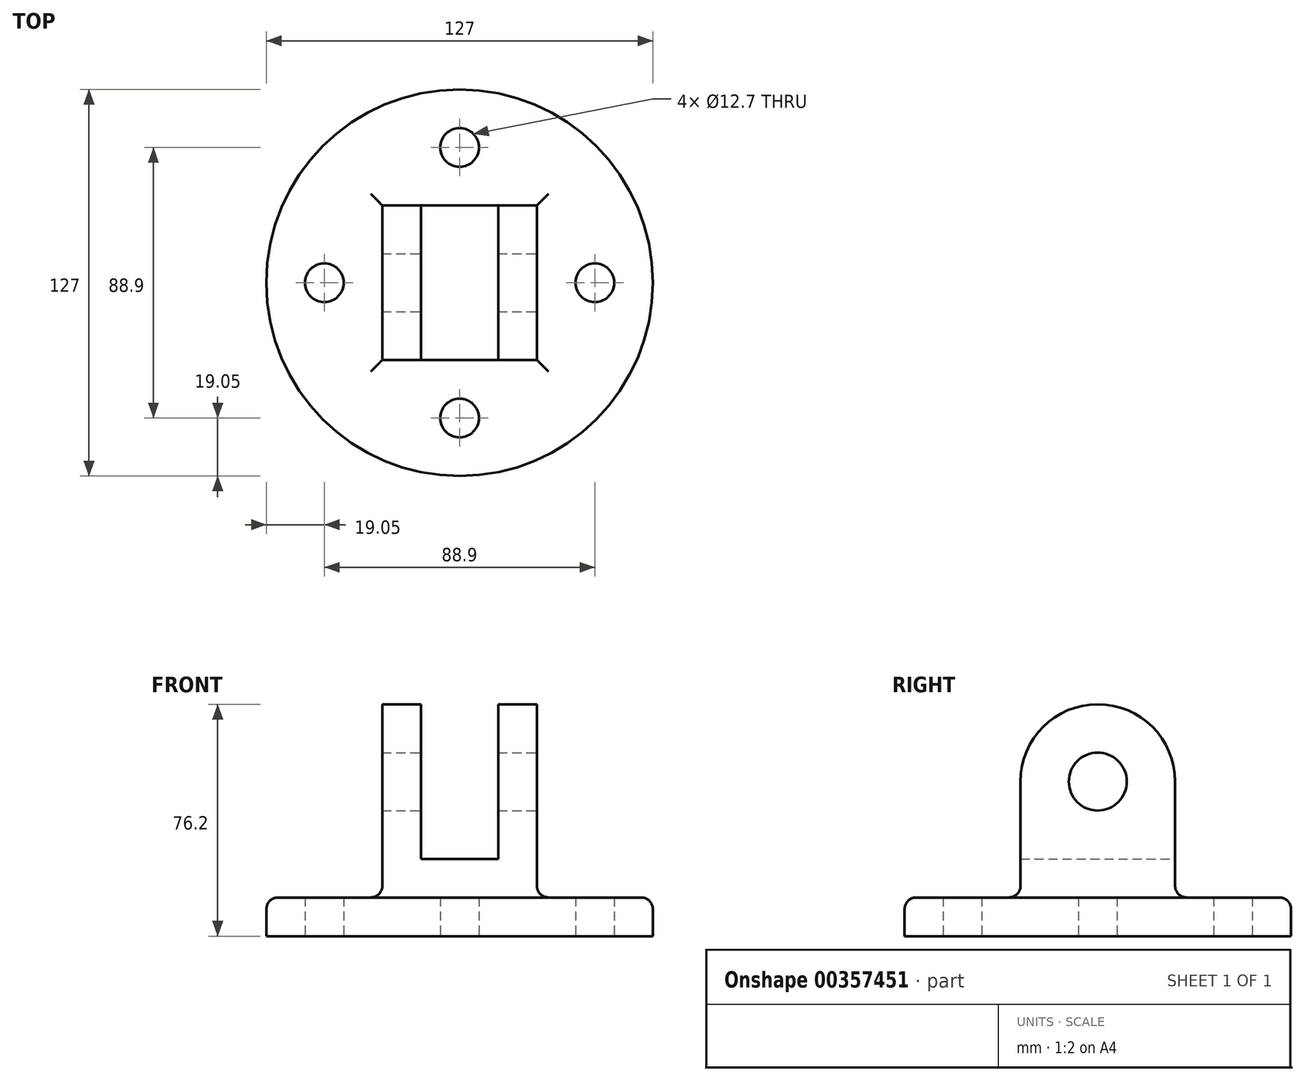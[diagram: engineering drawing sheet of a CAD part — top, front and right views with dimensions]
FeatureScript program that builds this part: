
annotation { "Feature Type Name" : "Feature", "Feature Type Description" : "" }
export const myFeature = defineFeature(function(context is Context, id is Id, definition is map)
    precondition{}
    {
        {
            var Q0;
            Q0=qCreatedBy(makeId("Top.planeOp"),FACE);
            var sketch = newSketch(context, id + "F0", { "sketchPlane" : qUnion([Q0])});
            skCircle(sketch, "E0", {"center": v(0, 0) * mm, "radius": 63.5 * mm});
            skCircle(sketch, "E1", {"center": v(-44.45, 0) * mm, "radius": 6.35 * mm});
            skCircle(sketch, "E2", {"center": v(44.45, 0) * mm, "radius": 6.35 * mm});
            skCircle(sketch, "E3", {"center": v(0, -44.45) * mm, "radius": 6.35 * mm});
            skCircle(sketch, "E4", {"center": v(0, 44.45) * mm, "radius": 6.35 * mm});
            skCircle(sketch, "E5", {"center": v(0, 0) * mm, "radius": 44.45 * mm, "construction": true});
            skSolve(sketch);
        }
        {
            var Q0;
            Q0 = qSketchRegion(id + "F0", true);
            extrude(context, id + "F1", {"entities" : qUnion([Q0]), "depth" : 12.7 * mm});
        }
        {
            var Q0;
            Q0=qCreatedBy(makeId("Front.planeOp"),FACE);
            var sketch = newSketch(context, id + "F2", { "sketchPlane" : qUnion([Q0])});
            skLineSegment(sketch, "E6", {"start": v(0, 70.09) * mm, "end": v(0, -41.11) * mm, "construction": true});
            skLineSegment(sketch, "E7", {"start": v(0, 0) * mm, "end": v(25.4, 0) * mm});
            skLineSegment(sketch, "E8", {"start": v(25.4, 0) * mm, "end": v(25.4, 76.2) * mm});
            skLineSegment(sketch, "E9", {"start": v(25.4, 76.2) * mm, "end": v(12.7, 76.2) * mm});
            skLineSegment(sketch, "E10", {"start": v(12.7, 76.2) * mm, "end": v(12.7, 25.4) * mm});
            skLineSegment(sketch, "E11", {"start": v(12.7, 25.4) * mm, "end": v(0, 25.4) * mm});
            skLineSegment(sketch, "E12.MirrorCS", {"start": v(-12.7, 25.4) * mm, "end": v(0, 25.4) * mm});
            skLineSegment(sketch, "E13.MirrorCS", {"start": v(-12.7, 76.2) * mm, "end": v(-12.7, 25.4) * mm});
            skLineSegment(sketch, "E14.MirrorCS", {"start": v(-25.4, 76.2) * mm, "end": v(-12.7, 76.2) * mm});
            skLineSegment(sketch, "E15.MirrorCS", {"start": v(-25.4, 0) * mm, "end": v(-25.4, 76.2) * mm});
            skLineSegment(sketch, "E16.MirrorCS", {"start": v(0, 0) * mm, "end": v(-25.4, 0) * mm});
            skSolve(sketch);
        }
        {
            var Q0;
            Q0 = qSketchRegion(id + "F2", true);
            extrude(context, id + "F3", {"entities" : qUnion([Q0]), "operationType" : NewBodyOperationType.ADD, "depth" : 25.4 * mm, "hasSecondDirection" : true, "secondDirectionOppositeDirection" : true, "secondDirectionDepth" : 25.4 * mm});
        }
        {
            var Q0;
            Q0=makeQuery(id+"F3.opExtrude","SWEPT_FACE",FACE,{"disambiguationData":[OSD([sQuery(id+"F2.wireOp",EDGE,"E8")])]});
            var sketch = newSketch(context, id + "F4", { "sketchPlane" : qUnion([Q0])});
            skCircle(sketch, "E17", {"center": v(0, 50.8) * mm, "radius": 9.53 * mm});
            skLineSegment(sketch, "E18", {"start": v(-25.4, 12.7) * mm, "end": v(-25.4, 50.8) * mm});
            skLineSegment(sketch, "E19", {"start": v(25.4, 50.8) * mm, "end": v(25.4, 12.7) * mm});
            skArc(sketch, "E20", {"start": v(25.4, 50.8) * mm, "mid": v(0, 76.2) * mm, "end": v(-25.4, 50.8) * mm});
            skSolve(sketch);
        }
        {
            var Q0;
            {var subQ0=sQuery(id+"F4.wireOp",EDGE,"BjLaF9JT-NZkI-fhuH-g375-j2dNAu3l2f7L");var subQ1=sQuery(id+"F2.wireOp",EDGE,"E8");var subQ2=makeQuery(id+"F3.opExtrude","CAP_EDGE",EDGE,{"disambiguationData":[OSD([subQ1])],"isStart":true});var subQ3=makeQuery(id+"F4.imprint","INTERSECT",VERTEX,{"derivedFrom":[subQ2,sQuery(id+"F4.wireOp",EDGE,"E19"),subQ0]});Q0=makeQuery(id+"F4.imprint","IMPRINT",FACE,{"disambiguationData":[TD([[makeQuery(id+"F4.imprint","IMPRINT",EDGE,{"disambiguationData":[TD([[subQ3,-1.0]])],"derivedFrom":subQ0}),-1.0]])]});}
            var Q1;
            {var subQ0=sQuery(id+"F4.wireOp",EDGE,"BjLaF9JT-NZkI-fhuH-g375-j2dNAu3l2f7L");var subQ1=sQuery(id+"F2.wireOp",EDGE,"E8");var subQ2=makeQuery(id+"F3.opExtrude","CAP_EDGE",EDGE,{"disambiguationData":[OSD([subQ1])],"isStart":false});var subQ3=makeQuery(id+"F4.imprint","INTERSECT",VERTEX,{"derivedFrom":[subQ2,sQuery(id+"F4.wireOp",EDGE,"E18"),subQ0]});Q1=makeQuery(id+"F4.imprint","IMPRINT",FACE,{"disambiguationData":[TD([[makeQuery(id+"F4.imprint","IMPRINT",EDGE,{"disambiguationData":[TD([[subQ3,1.0]])],"derivedFrom":subQ0}),-1.0]])]});}
            var Q2;
            Q2=makeQuery(id+"F4.imprint","IMPRINT",FACE,{"disambiguationData":[TD([[makeQuery(id+"F4.imprint","IMPRINT",EDGE,{"derivedFrom":sQuery(id+"F4.wireOp",EDGE,"E17")}),1.0]])]});
            extrude(context, id + "F5", {"entities" : qUnion([Q0, Q1, Q2]), "operationType" : NewBodyOperationType.REMOVE, "endBound" : BoundingType.THROUGH_ALL, "oppositeDirection" : true, "depth" : 25.4 * mm});
        }
        {
            var Q0;
            {var subQ0=sQuery(id+"F4.wireOp",EDGE,"E20");var subQ1=sQuery(id+"F2.wireOp",EDGE,"E8");var subQ2=makeQuery(id+"F3.opExtrude","CAP_EDGE",EDGE,{"disambiguationData":[OSD([subQ1])],"isStart":false});var subQ3=makeQuery(id+"F4.imprint","INTERSECT",VERTEX,{"derivedFrom":[subQ2,sQuery(id+"F4.wireOp",EDGE,"E18"),subQ0]});Q0=makeQuery(id+"F4.imprint","IMPRINT",FACE,{"disambiguationData":[TD([[makeQuery(id+"F4.imprint","IMPRINT",EDGE,{"disambiguationData":[TD([[subQ3,1.0]])],"derivedFrom":subQ0}),-1.0]])]});}
            var Q1;
            {var subQ0=sQuery(id+"F4.wireOp",EDGE,"E20");var subQ1=sQuery(id+"F2.wireOp",EDGE,"E8");var subQ2=makeQuery(id+"F3.opExtrude","CAP_EDGE",EDGE,{"disambiguationData":[OSD([subQ1])],"isStart":true});var subQ3=makeQuery(id+"F4.imprint","INTERSECT",VERTEX,{"derivedFrom":[subQ2,sQuery(id+"F4.wireOp",EDGE,"E19"),subQ0]});Q1=makeQuery(id+"F4.imprint","IMPRINT",FACE,{"disambiguationData":[TD([[makeQuery(id+"F4.imprint","IMPRINT",EDGE,{"disambiguationData":[TD([[subQ3,-1.0]])],"derivedFrom":subQ0}),-1.0]])]});}
            extrude(context, id + "F6", {"entities" : qUnion([Q0, Q1]), "operationType" : NewBodyOperationType.REMOVE, "endBound" : BoundingType.THROUGH_ALL, "oppositeDirection" : true, "depth" : 25.4 * mm});
        }
        {
            var Q0;
            Q0=makeQuery(id+"F1.opExtrude","CAP_EDGE",EDGE,{"disambiguationData":[OSD([sQuery(id+"F0.wireOp",EDGE,"E0")])],"isStart":false});
            fillet(context, id + "F7", {"entities" : qUnion([Q0]), "radius" : 3.8 * mm, "tangentPropagation" : true, "allowEdgeOverflow" : false});
        }
        {
            var Q0;
            Q0=makeQuery(id+"F3.boolean.opBoolean","INTERSECT",EDGE,{"derivedFrom":[makeQuery(id+"F1.opExtrude","CAP_FACE",FACE,{"disambiguationData":[OSD([sQuery(id+"F0.wireOp",EDGE,"E0"),sQuery(id+"F0.wireOp",EDGE,"E1"),sQuery(id+"F0.wireOp",EDGE,"E2"),sQuery(id+"F0.wireOp",EDGE,"E3"),sQuery(id+"F0.wireOp",EDGE,"E4")])],"isStart":false}),makeQuery(id+"F3.opExtrude","CAP_FACE",FACE,{"disambiguationData":[OSD([sQuery(id+"F2.wireOp",EDGE,"E7"),sQuery(id+"F2.wireOp",EDGE,"E8"),sQuery(id+"F2.wireOp",EDGE,"E9"),sQuery(id+"F2.wireOp",EDGE,"E10"),sQuery(id+"F2.wireOp",EDGE,"E11"),sQuery(id+"F2.wireOp",EDGE,"E12.MirrorCS"),sQuery(id+"F2.wireOp",EDGE,"E13.MirrorCS"),sQuery(id+"F2.wireOp",EDGE,"E14.MirrorCS"),sQuery(id+"F2.wireOp",EDGE,"E15.MirrorCS"),sQuery(id+"F2.wireOp",EDGE,"E16.MirrorCS")])],"isStart":false})]});
            var Q1;
            Q1=makeQuery(id+"F3.boolean.opBoolean","INTERSECT",EDGE,{"derivedFrom":[makeQuery(id+"F1.opExtrude","CAP_FACE",FACE,{"disambiguationData":[OSD([sQuery(id+"F0.wireOp",EDGE,"E0"),sQuery(id+"F0.wireOp",EDGE,"E1"),sQuery(id+"F0.wireOp",EDGE,"E2"),sQuery(id+"F0.wireOp",EDGE,"E3"),sQuery(id+"F0.wireOp",EDGE,"E4")])],"isStart":false}),makeQuery(id+"F3.opExtrude","SWEPT_FACE",FACE,{"disambiguationData":[OSD([sQuery(id+"F2.wireOp",EDGE,"E8")])]})]});
            var Q2;
            Q2=makeQuery(id+"F3.boolean.opBoolean","INTERSECT",EDGE,{"derivedFrom":[makeQuery(id+"F1.opExtrude","CAP_FACE",FACE,{"disambiguationData":[OSD([sQuery(id+"F0.wireOp",EDGE,"E0"),sQuery(id+"F0.wireOp",EDGE,"E1"),sQuery(id+"F0.wireOp",EDGE,"E2"),sQuery(id+"F0.wireOp",EDGE,"E3"),sQuery(id+"F0.wireOp",EDGE,"E4")])],"isStart":false}),makeQuery(id+"F3.opExtrude","CAP_FACE",FACE,{"disambiguationData":[OSD([sQuery(id+"F2.wireOp",EDGE,"E7"),sQuery(id+"F2.wireOp",EDGE,"E8"),sQuery(id+"F2.wireOp",EDGE,"E9"),sQuery(id+"F2.wireOp",EDGE,"E10"),sQuery(id+"F2.wireOp",EDGE,"E11"),sQuery(id+"F2.wireOp",EDGE,"E12.MirrorCS"),sQuery(id+"F2.wireOp",EDGE,"E13.MirrorCS"),sQuery(id+"F2.wireOp",EDGE,"E14.MirrorCS"),sQuery(id+"F2.wireOp",EDGE,"E15.MirrorCS"),sQuery(id+"F2.wireOp",EDGE,"E16.MirrorCS")])],"isStart":true})]});
            var Q3;
            Q3=makeQuery(id+"F3.boolean.opBoolean","INTERSECT",EDGE,{"derivedFrom":[makeQuery(id+"F1.opExtrude","CAP_FACE",FACE,{"disambiguationData":[OSD([sQuery(id+"F0.wireOp",EDGE,"E0"),sQuery(id+"F0.wireOp",EDGE,"E1"),sQuery(id+"F0.wireOp",EDGE,"E2"),sQuery(id+"F0.wireOp",EDGE,"E3"),sQuery(id+"F0.wireOp",EDGE,"E4")])],"isStart":false}),makeQuery(id+"F3.opExtrude","SWEPT_FACE",FACE,{"disambiguationData":[OSD([sQuery(id+"F2.wireOp",EDGE,"E15.MirrorCS")])]})]});
            fillet(context, id + "F8", {"entities" : qUnion([Q0, Q1, Q2, Q3]), "radius" : 3.8 * mm, "tangentPropagation" : true, "allowEdgeOverflow" : false});
        }
    });
